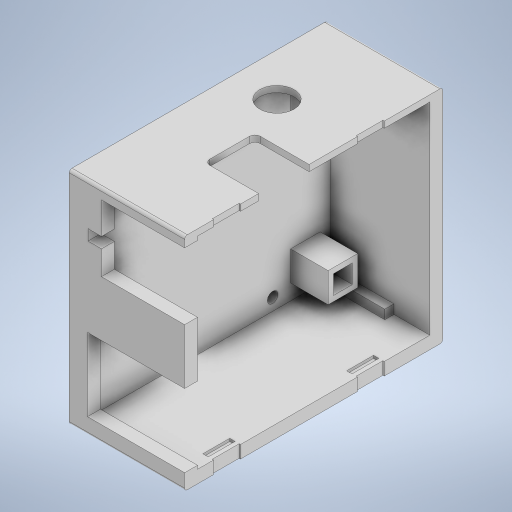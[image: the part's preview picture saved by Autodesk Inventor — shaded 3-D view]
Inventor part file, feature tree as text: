
AUTODESK INVENTOR PART (.ipt)
format: ipt  version: 2023 (Build 270158030, 158C)  size: 839,680 bytes
history: native  units: mm
features: sketch x20, extrude x19, fillet x2, emboss x1
ambient origin geometry x8: Origin, YZ Plane, XZ Plane, XY Plane, X Axis, Y Axis, Z Axis, Center Point
bodies: Solid1 (feature_tree)
feature tree (42):
  extrude  "BasePlate"  Depth=48.11mm
  extrude  "Walls"  Depth=2.0mm
  extrude  "USB-C"  Depth=2.4mm
  extrude  "PowerConnector1"  Depth=18.5mm TaperAngle=0.0deg
  extrude  "PowerConnector2"  Depth=13.8mm
  extrude  "RJ-12"  Depth=12.4mm
  extrude  "ZBButton"  Depth=15.5mm TaperAngle=0.0deg
  extrude  "ResetButton"  Depth=2.0mm
  extrude  "ButtonFuehrung"  Depth=2.5mm TaperAngle=0.0deg
  extrude  "LED"  Depth=3.0mm
  extrude  "Antenna"  Depth=3.5mm
  extrude  "Extrusion12"  Depth=5.35mm
  extrude  "Extrusion13"  Depth=3.0mm TaperAngle=0.0deg
  extrude  "Extrusion14"  Depth=3.5mm
  extrude  "Extrusion15"  Depth=6.05mm
  fillet  "Fillet2"  Radius=3.0mm
  emboss  "Emboss1"
  extrude  "Oeffnungskerben1"  Depth=5.5mm
  extrude  "Oeffnugskerben2"  Depth=1.0mm
  extrude  "TrimmWall"  Depth=5.5mm
  fillet  "Fillet3"  Radius=1.0mm
  extrude  "PCBHolder"  Depth=1.0mm TaperAngle=0.0deg
  sketch  "Sketch1"  dims[d0=42.0mm d1=48.11mm]
  sketch  "Sketch3"  dims[d2=3.0mm d3=0.0mm d4=2.0mm]
  sketch  "Sketch4"  dims[d5=2.35mm d6=2.4mm]
  sketch  "Sketch5"  dims[d7=2.4mm d8=18.5mm d9=0.0mm]
  sketch  "Sketch6"  dims[d10=9.4mm d11=13.8mm]
  sketch  "Sketch8"  dims[d12=10.1mm d13=0.0mm d14=12.4mm]
  sketch  "Sketch9"  dims[d15=2.7mm d16=15.5mm d17=0.0mm]
  sketch  "Sketch10"  dims[d18=2.4mm d19=2.0mm]
  sketch  "Sketch11"  dims[d20=5.9mm d21=2.5mm d22=0.0mm]
  sketch  "Sketch12"  dims[d23=13.6mm d24=3.0mm]
  sketch  "Sketch13"  dims[d25=18.1mm d26=0.0mm d28=3.5mm]
  sketch  "Sketch14"  dims[d29=3.5mm d30=5.35mm]
  sketch  "Sketch15"  dims[d31=6.25mm d32=3.0mm d33=0.0mm]
  sketch  "Sketch16"  dims[d34=3.5mm d35=3.5mm]
  sketch  "Sketch17"  dims[d36=5.35mm d37=6.05mm d38=3.0mm d39=0.0mm]
  sketch  "Sketch18"  dims[d40=5.5mm d41=5.5mm]
  sketch  "Sketch23"  dims[d42=1.0mm d43=1.0mm]
  sketch  "Sketch24"  dims[d44=5.5mm d45=5.5mm d46=1.0mm]
  sketch  "Sketch25"  dims[d47=1.0mm d48=7.0mm d49=0.0mm]
  sketch  "Sketch26"  dims[d50=2.0mm d51=4.6mm d52=13.2mm d53=3.0mm d54=0.0mm d55=6.4mm d56=8.0mm d58=2.0mm d59=0.0mm d60=1.0mm d61=5.0mm d62=1.0mm d63=5.5mm d64=0.5mm d65=0.0mm d66=1.0mm d67=5.0mm d68=1.0mm d69=11.0mm d70=0.5mm d71=0.0mm d72=1.0mm d73=5.0mm d74=1.0mm d75=5.5mm d76=0.5mm d77=0.0mm d78=1.0mm d79=5.0mm d80=1.0mm d81=11.0mm d82=0.5mm d83=0.0mm d84=1.0mm d85=0.25mm d86=0.25mm d87=1.0mm d88=0.0mm d97=0.25mm d98=5.0mm d99=0.0mm d100=0.25mm d101=5.0mm d102=0.0mm d103=0.0mm d104=0.0mm d105=0.25mm d106=5.0mm d107=0.0mm d108=0.25mm d109=5.0mm d110=0.0mm d111=0.0mm d112=0.0mm d114=17.4mm d115=0.83mm d116=0.0mm d117=0.5mm d118=1.7mm d119=1.7mm d120=1.7mm d121=1.7mm d122=11.8mm d123=0.0mm]
